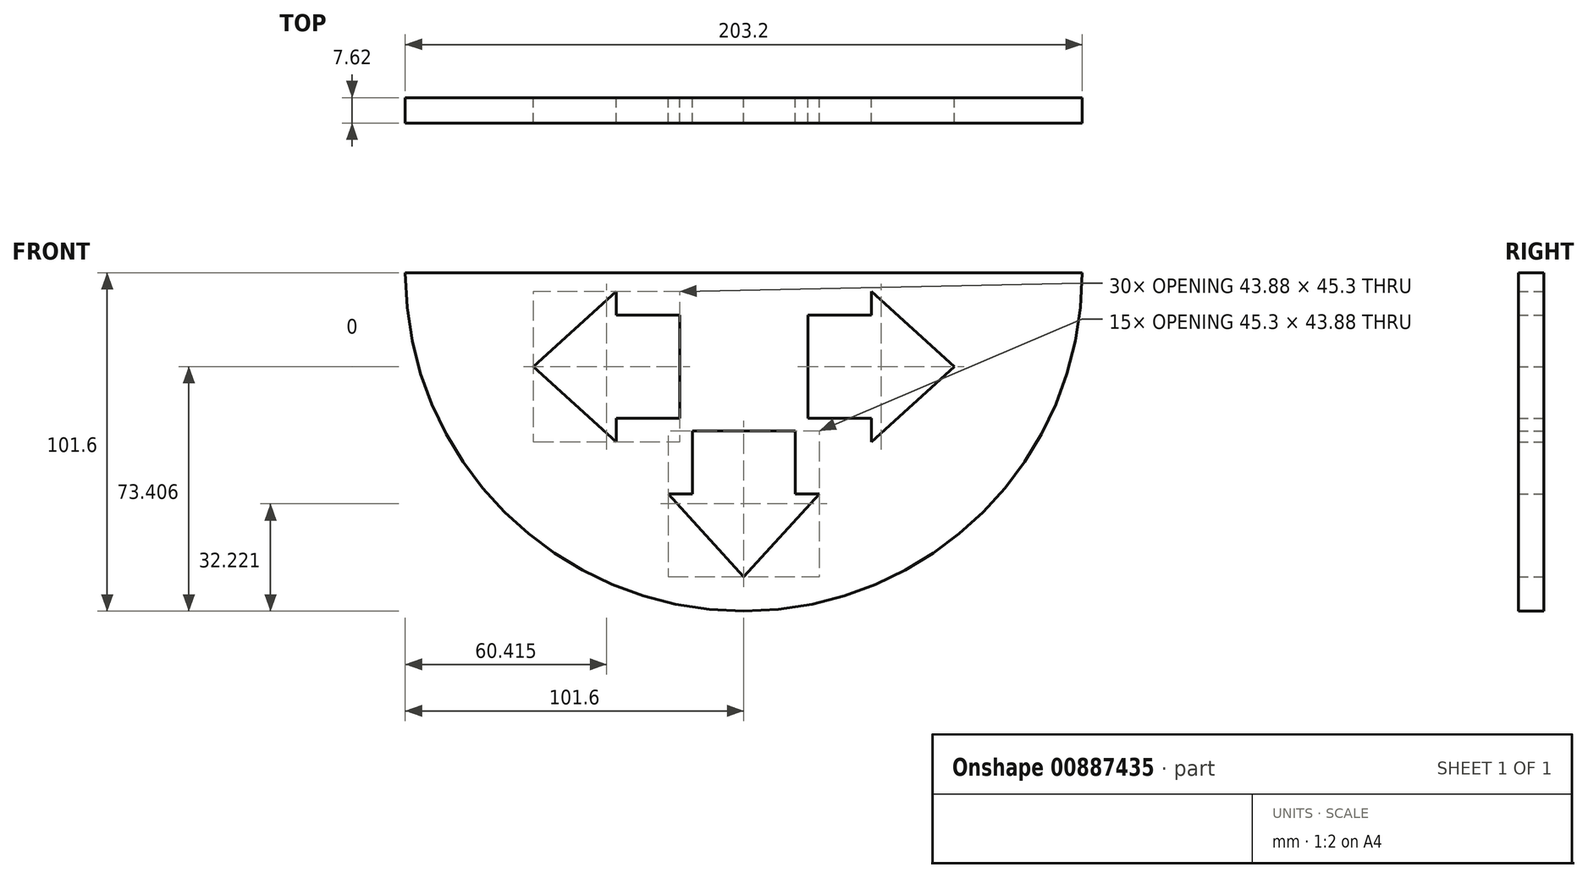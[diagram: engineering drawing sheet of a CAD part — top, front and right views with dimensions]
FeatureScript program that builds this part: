
annotation { "Feature Type Name" : "Feature", "Feature Type Description" : "" }
export const myFeature = defineFeature(function(context is Context, id is Id, definition is map)
    precondition{}
    {
        {
            var Q0;
            Q0=qCreatedBy(makeId("Front.planeOp"),FACE);
            var sketch = newSketch(context, id + "F0", { "sketchPlane" : qUnion([Q0])});
            skLineSegment(sketch, "E0", {"start": v(0, 0) * mm, "end": v(101.6, 0) * mm});
            skLineSegment(sketch, "E1", {"start": v(0, 0) * mm, "end": v(-101.6, 0) * mm});
            skArc(sketch, "E2", {"start": v(101.6, 0) * mm, "mid": v(0, -101.6) * mm, "end": v(-101.6, 0) * mm});
            skLineSegment(sketch, "E3", {"start": v(0, -91.32) * mm, "end": v(22.65, -66.42) * mm});
            skLineSegment(sketch, "E4", {"start": v(22.65, -66.42) * mm, "end": v(15.5, -66.42) * mm});
            skLineSegment(sketch, "E5", {"start": v(15.5, -66.42) * mm, "end": v(15.5, -47.44) * mm});
            skLineSegment(sketch, "E6", {"start": v(15.5, -47.44) * mm, "end": v(0, -47.44) * mm});
            skLineSegment(sketch, "E7.MirrorCS", {"start": v(0, -91.32) * mm, "end": v(-22.65, -66.42) * mm});
            skLineSegment(sketch, "E8.MirrorCS", {"start": v(-22.65, -66.42) * mm, "end": v(-15.5, -66.42) * mm});
            skLineSegment(sketch, "E9.MirrorCS", {"start": v(-15.5, -47.44) * mm, "end": v(0, -47.44) * mm});
            skLineSegment(sketch, "E10.MirrorCS", {"start": v(-15.5, -66.42) * mm, "end": v(-15.5, -47.44) * mm});
            skLineSegment(sketch, "E11", {"start": v(0, -47.44) * mm, "end": v(0, -30.64) * mm});
            skLineSegment(sketch, "E12.1.0", {"start": v(19.25, -12.7) * mm, "end": v(19.25, -28.2) * mm});
            skLineSegment(sketch, "E12.1.1", {"start": v(19.25, -43.69) * mm, "end": v(19.25, -28.2) * mm});
            skLineSegment(sketch, "E12.1.2", {"start": v(38.23, -43.69) * mm, "end": v(19.25, -43.69) * mm});
            skLineSegment(sketch, "E12.1.3", {"start": v(38.23, -50.84) * mm, "end": v(38.23, -43.69) * mm});
            skLineSegment(sketch, "E12.1.4", {"start": v(63.12, -28.2) * mm, "end": v(38.23, -50.84) * mm});
            skLineSegment(sketch, "E12.1.5", {"start": v(63.12, -28.2) * mm, "end": v(38.23, -5.54) * mm});
            skLineSegment(sketch, "E12.1.6", {"start": v(38.23, -5.54) * mm, "end": v(38.23, -12.7) * mm});
            skLineSegment(sketch, "E12.1.7", {"start": v(38.23, -12.7) * mm, "end": v(19.25, -12.7) * mm});
            skLineSegment(sketch, "E12.3.0", {"start": v(-19.25, -43.69) * mm, "end": v(-19.25, -28.2) * mm});
            skLineSegment(sketch, "E12.3.1", {"start": v(-19.25, -12.7) * mm, "end": v(-19.25, -28.2) * mm});
            skLineSegment(sketch, "E12.3.2", {"start": v(-38.23, -12.7) * mm, "end": v(-19.25, -12.7) * mm});
            skLineSegment(sketch, "E12.3.3", {"start": v(-38.23, -5.54) * mm, "end": v(-38.23, -12.7) * mm});
            skLineSegment(sketch, "E12.3.4", {"start": v(-63.12, -28.2) * mm, "end": v(-38.23, -5.54) * mm});
            skLineSegment(sketch, "E12.3.5", {"start": v(-63.12, -28.2) * mm, "end": v(-38.23, -50.84) * mm});
            skLineSegment(sketch, "E12.3.6", {"start": v(-38.23, -50.84) * mm, "end": v(-38.23, -43.69) * mm});
            skLineSegment(sketch, "E12.3.7", {"start": v(-38.23, -43.69) * mm, "end": v(-19.25, -43.69) * mm});
            skPoint(sketch, "E12.center", {"position": v(0, -28.2) * mm});
            skSolve(sketch);
        }
        {
            var Q0;
            Q0=makeQuery(id+"F0.imprint","IMPRINT",FACE,{"disambiguationData":[TD([[makeQuery(id+"F0.imprint","IMPRINT",EDGE,{"derivedFrom":sQuery(id+"F0.wireOp",EDGE,"E0")}),-1.0]])]});
            extrude(context, id + "F1", {"entities" : qUnion([Q0]), "depth" : 7.62 * mm, "offsetDistance" : 25.4 * mm});
        }
    });
